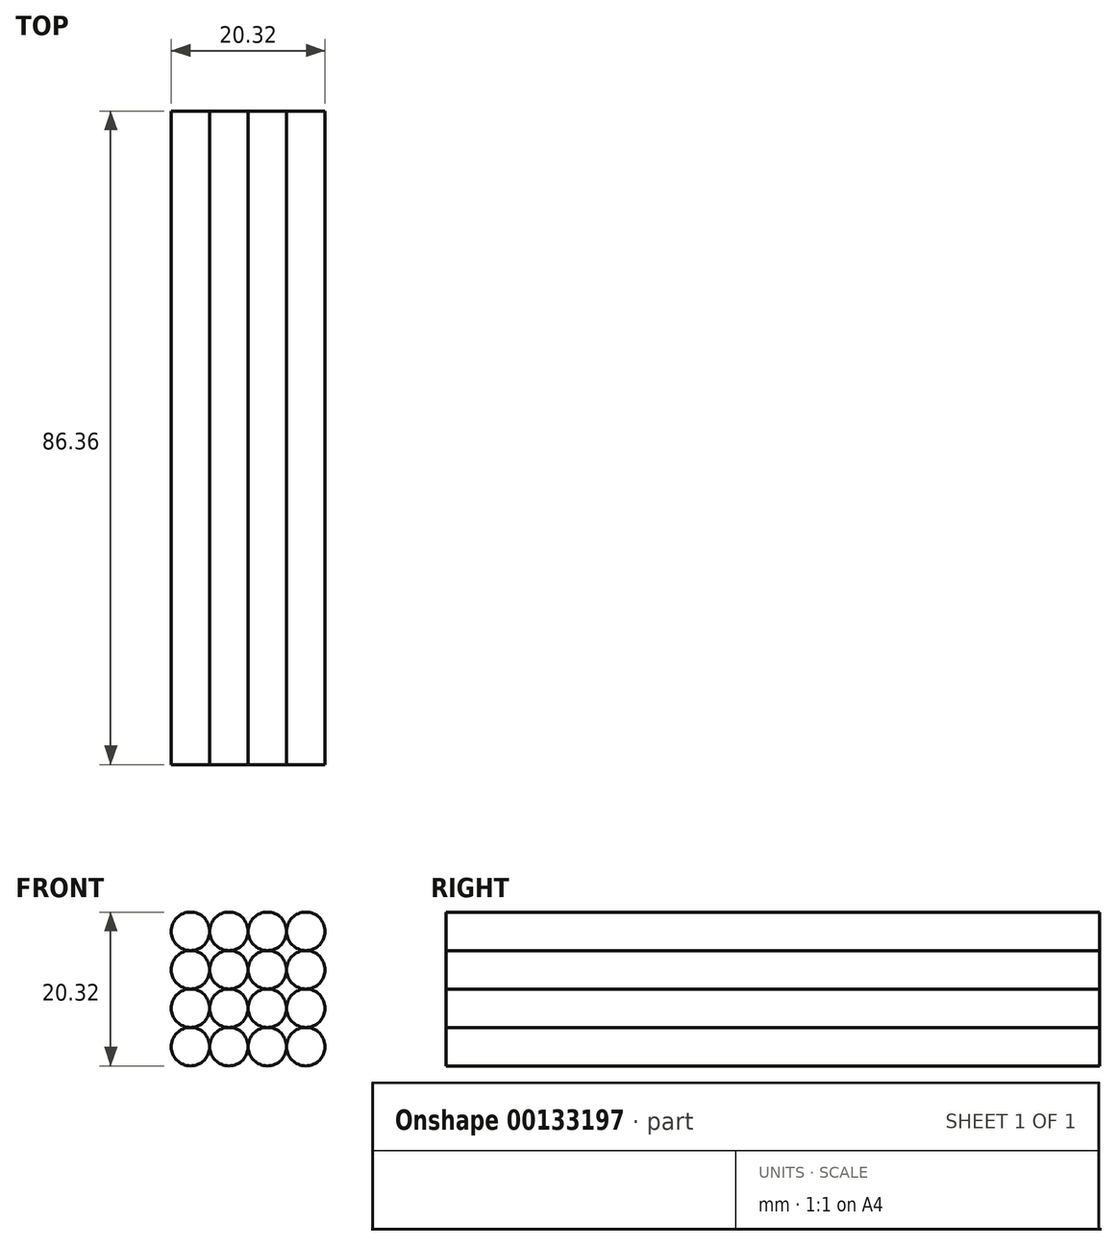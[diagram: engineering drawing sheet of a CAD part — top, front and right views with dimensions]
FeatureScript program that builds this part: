
annotation { "Feature Type Name" : "Feature", "Feature Type Description" : "" }
export const myFeature = defineFeature(function(context is Context, id is Id, definition is map)
    precondition{}
    {
        {
            var Q0;
            Q0=qCreatedBy(makeId("Front.planeOp"),FACE);
            var sketch = newSketch(context, id + "F0", { "sketchPlane" : qUnion([Q0])});
            skCircle(sketch, "E0", {"center": v(0, 0) * mm, "radius": 2.54 * mm});
            skCircle(sketch, "E1.0.1.0", {"center": v(0, 5.08) * mm, "radius": 2.54 * mm});
            skCircle(sketch, "E1.0.2.0", {"center": v(0, 10.16) * mm, "radius": 2.54 * mm});
            skCircle(sketch, "E1.0.3.0", {"center": v(0, 15.24) * mm, "radius": 2.54 * mm});
            skCircle(sketch, "E1.1.0.0", {"center": v(5.08, 0) * mm, "radius": 2.54 * mm});
            skCircle(sketch, "E1.1.1.0", {"center": v(5.08, 5.08) * mm, "radius": 2.54 * mm});
            skCircle(sketch, "E1.1.2.0", {"center": v(5.08, 10.16) * mm, "radius": 2.54 * mm});
            skCircle(sketch, "E1.1.3.0", {"center": v(5.08, 15.24) * mm, "radius": 2.54 * mm});
            skCircle(sketch, "E1.2.0.0", {"center": v(10.16, 0) * mm, "radius": 2.54 * mm});
            skCircle(sketch, "E1.2.1.0", {"center": v(10.16, 5.08) * mm, "radius": 2.54 * mm});
            skCircle(sketch, "E1.2.2.0", {"center": v(10.16, 10.16) * mm, "radius": 2.54 * mm});
            skCircle(sketch, "E1.2.3.0", {"center": v(10.16, 15.24) * mm, "radius": 2.54 * mm});
            skCircle(sketch, "E1.3.0.0", {"center": v(15.24, 0) * mm, "radius": 2.54 * mm});
            skCircle(sketch, "E1.3.1.0", {"center": v(15.24, 5.08) * mm, "radius": 2.54 * mm});
            skCircle(sketch, "E1.3.2.0", {"center": v(15.24, 10.16) * mm, "radius": 2.54 * mm});
            skCircle(sketch, "E1.3.3.0", {"center": v(15.24, 15.24) * mm, "radius": 2.54 * mm});
            skLineSegment(sketch, "E1.direction1", {"start": v(0, 0) * mm, "end": v(5.08, 0) * mm, "construction": true});
            skLineSegment(sketch, "E1.direction2", {"start": v(0, 0) * mm, "end": v(0, 5.08) * mm, "construction": true});
            skSolve(sketch);
        }
        {
            var Q0;
            {var subQ0=sQuery(id+"F0.wireOp",EDGE,"E0");var subQ1=makeQuery(id+"F0.imprint","INTERSECT",VERTEX,{"derivedFrom":[subQ0,sQuery(id+"F0.wireOp",EDGE,"E1.0.1.0")]});Q0=makeQuery(id+"F0.imprint","IMPRINT",FACE,{"disambiguationData":[TD([[makeQuery(id+"F0.imprint","IMPRINT",EDGE,{"disambiguationData":[TD([[subQ1,1.0]])],"derivedFrom":subQ0}),1.0]])]});}
            var Q1;
            {var subQ0=sQuery(id+"F0.wireOp",EDGE,"E1.0.3.0");var subQ1=makeQuery(id+"F0.imprint","INTERSECT",VERTEX,{"derivedFrom":[sQuery(id+"F0.wireOp",EDGE,"E1.0.2.0"),subQ0]});Q1=makeQuery(id+"F0.imprint","IMPRINT",FACE,{"disambiguationData":[TD([[makeQuery(id+"F0.imprint","IMPRINT",EDGE,{"disambiguationData":[TD([[subQ1,1.0]])],"derivedFrom":subQ0}),1.0]])]});}
            var Q2;
            {var subQ0=sQuery(id+"F0.wireOp",EDGE,"E1.3.0.0");var subQ1=makeQuery(id+"F0.imprint","INTERSECT",VERTEX,{"derivedFrom":[sQuery(id+"F0.wireOp",EDGE,"E1.2.0.0"),subQ0]});Q2=makeQuery(id+"F0.imprint","IMPRINT",FACE,{"disambiguationData":[TD([[makeQuery(id+"F0.imprint","IMPRINT",EDGE,{"disambiguationData":[TD([[subQ1,1.0]])],"derivedFrom":subQ0}),1.0]])]});}
            var Q3;
            {var subQ0=sQuery(id+"F0.wireOp",EDGE,"E1.3.3.0");var subQ1=makeQuery(id+"F0.imprint","INTERSECT",VERTEX,{"derivedFrom":[sQuery(id+"F0.wireOp",EDGE,"E1.2.3.0"),subQ0]});Q3=makeQuery(id+"F0.imprint","IMPRINT",FACE,{"disambiguationData":[TD([[makeQuery(id+"F0.imprint","IMPRINT",EDGE,{"disambiguationData":[TD([[subQ1,-1.0]])],"derivedFrom":subQ0}),1.0]])]});}
            var Q4;
            {var subQ0=sQuery(id+"F0.wireOp",EDGE,"E1.0.1.0");var subQ1=makeQuery(id+"F0.imprint","INTERSECT",VERTEX,{"derivedFrom":[subQ0,sQuery(id+"F0.wireOp",EDGE,"E1.0.2.0")]});Q4=makeQuery(id+"F0.imprint","IMPRINT",FACE,{"disambiguationData":[TD([[makeQuery(id+"F0.imprint","IMPRINT",EDGE,{"disambiguationData":[TD([[subQ1,1.0]])],"derivedFrom":subQ0}),1.0]])]});}
            var Q5;
            {var subQ0=sQuery(id+"F0.wireOp",EDGE,"E1.0.2.0");var subQ1=makeQuery(id+"F0.imprint","INTERSECT",VERTEX,{"derivedFrom":[subQ0,sQuery(id+"F0.wireOp",EDGE,"E1.0.3.0")]});Q5=makeQuery(id+"F0.imprint","IMPRINT",FACE,{"disambiguationData":[TD([[makeQuery(id+"F0.imprint","IMPRINT",EDGE,{"disambiguationData":[TD([[subQ1,1.0]])],"derivedFrom":subQ0}),1.0]])]});}
            var Q6;
            {var subQ0=sQuery(id+"F0.wireOp",EDGE,"E1.1.0.0");var subQ1=makeQuery(id+"F0.imprint","INTERSECT",VERTEX,{"derivedFrom":[subQ0,sQuery(id+"F0.wireOp",EDGE,"E1.2.0.0")]});Q6=makeQuery(id+"F0.imprint","IMPRINT",FACE,{"disambiguationData":[TD([[makeQuery(id+"F0.imprint","IMPRINT",EDGE,{"disambiguationData":[TD([[subQ1,-1.0]])],"derivedFrom":subQ0}),1.0]])]});}
            var Q7;
            {var subQ0=sQuery(id+"F0.wireOp",EDGE,"E1.1.3.0");var subQ1=makeQuery(id+"F0.imprint","INTERSECT",VERTEX,{"derivedFrom":[sQuery(id+"F0.wireOp",EDGE,"E1.0.3.0"),subQ0]});Q7=makeQuery(id+"F0.imprint","IMPRINT",FACE,{"disambiguationData":[TD([[makeQuery(id+"F0.imprint","IMPRINT",EDGE,{"disambiguationData":[TD([[subQ1,1.0]])],"derivedFrom":subQ0}),1.0]])]});}
            var Q8;
            {var subQ0=sQuery(id+"F0.wireOp",EDGE,"E1.2.0.0");var subQ1=makeQuery(id+"F0.imprint","INTERSECT",VERTEX,{"derivedFrom":[subQ0,sQuery(id+"F0.wireOp",EDGE,"E1.3.0.0")]});Q8=makeQuery(id+"F0.imprint","IMPRINT",FACE,{"disambiguationData":[TD([[makeQuery(id+"F0.imprint","IMPRINT",EDGE,{"disambiguationData":[TD([[subQ1,-1.0]])],"derivedFrom":subQ0}),1.0]])]});}
            var Q9;
            {var subQ0=sQuery(id+"F0.wireOp",EDGE,"E1.2.3.0");var subQ1=makeQuery(id+"F0.imprint","INTERSECT",VERTEX,{"derivedFrom":[sQuery(id+"F0.wireOp",EDGE,"E1.1.3.0"),subQ0]});Q9=makeQuery(id+"F0.imprint","IMPRINT",FACE,{"disambiguationData":[TD([[makeQuery(id+"F0.imprint","IMPRINT",EDGE,{"disambiguationData":[TD([[subQ1,1.0]])],"derivedFrom":subQ0}),1.0]])]});}
            var Q10;
            {var subQ0=sQuery(id+"F0.wireOp",EDGE,"E1.3.1.0");var subQ1=makeQuery(id+"F0.imprint","INTERSECT",VERTEX,{"derivedFrom":[subQ0,sQuery(id+"F0.wireOp",EDGE,"E1.3.2.0")]});Q10=makeQuery(id+"F0.imprint","IMPRINT",FACE,{"disambiguationData":[TD([[makeQuery(id+"F0.imprint","IMPRINT",EDGE,{"disambiguationData":[TD([[subQ1,-1.0]])],"derivedFrom":subQ0}),1.0]])]});}
            var Q11;
            {var subQ0=sQuery(id+"F0.wireOp",EDGE,"E1.3.2.0");var subQ1=makeQuery(id+"F0.imprint","INTERSECT",VERTEX,{"derivedFrom":[subQ0,sQuery(id+"F0.wireOp",EDGE,"E1.3.3.0")]});Q11=makeQuery(id+"F0.imprint","IMPRINT",FACE,{"disambiguationData":[TD([[makeQuery(id+"F0.imprint","IMPRINT",EDGE,{"disambiguationData":[TD([[subQ1,-1.0]])],"derivedFrom":subQ0}),1.0]])]});}
            var Q12;
            {var subQ0=sQuery(id+"F0.wireOp",EDGE,"E1.2.1.0");var subQ1=makeQuery(id+"F0.imprint","INTERSECT",VERTEX,{"derivedFrom":[subQ0,sQuery(id+"F0.wireOp",EDGE,"E1.2.2.0")]});Q12=makeQuery(id+"F0.imprint","IMPRINT",FACE,{"disambiguationData":[TD([[makeQuery(id+"F0.imprint","IMPRINT",EDGE,{"disambiguationData":[TD([[subQ1,1.0]])],"derivedFrom":subQ0}),1.0]])]});}
            var Q13;
            {var subQ0=sQuery(id+"F0.wireOp",EDGE,"E1.1.1.0");var subQ1=makeQuery(id+"F0.imprint","INTERSECT",VERTEX,{"derivedFrom":[subQ0,sQuery(id+"F0.wireOp",EDGE,"E1.1.2.0")]});Q13=makeQuery(id+"F0.imprint","IMPRINT",FACE,{"disambiguationData":[TD([[makeQuery(id+"F0.imprint","IMPRINT",EDGE,{"disambiguationData":[TD([[subQ1,1.0]])],"derivedFrom":subQ0}),1.0]])]});}
            var Q14;
            {var subQ0=sQuery(id+"F0.wireOp",EDGE,"E1.2.2.0");var subQ1=makeQuery(id+"F0.imprint","INTERSECT",VERTEX,{"derivedFrom":[subQ0,sQuery(id+"F0.wireOp",EDGE,"E1.2.3.0")]});Q14=makeQuery(id+"F0.imprint","IMPRINT",FACE,{"disambiguationData":[TD([[makeQuery(id+"F0.imprint","IMPRINT",EDGE,{"disambiguationData":[TD([[subQ1,1.0]])],"derivedFrom":subQ0}),1.0]])]});}
            var Q15;
            {var subQ0=sQuery(id+"F0.wireOp",EDGE,"E1.1.2.0");var subQ1=makeQuery(id+"F0.imprint","INTERSECT",VERTEX,{"derivedFrom":[subQ0,sQuery(id+"F0.wireOp",EDGE,"E1.1.3.0")]});Q15=makeQuery(id+"F0.imprint","IMPRINT",FACE,{"disambiguationData":[TD([[makeQuery(id+"F0.imprint","IMPRINT",EDGE,{"disambiguationData":[TD([[subQ1,1.0]])],"derivedFrom":subQ0}),1.0]])]});}
            extrude(context, id + "F1", {"entities" : qUnion([Q0, Q1, Q2, Q3, Q4, Q5, Q6, Q7, Q8, Q9, Q10, Q11, Q12, Q13, Q14, Q15]), "depth" : 86.36 * mm});
        }
    });
